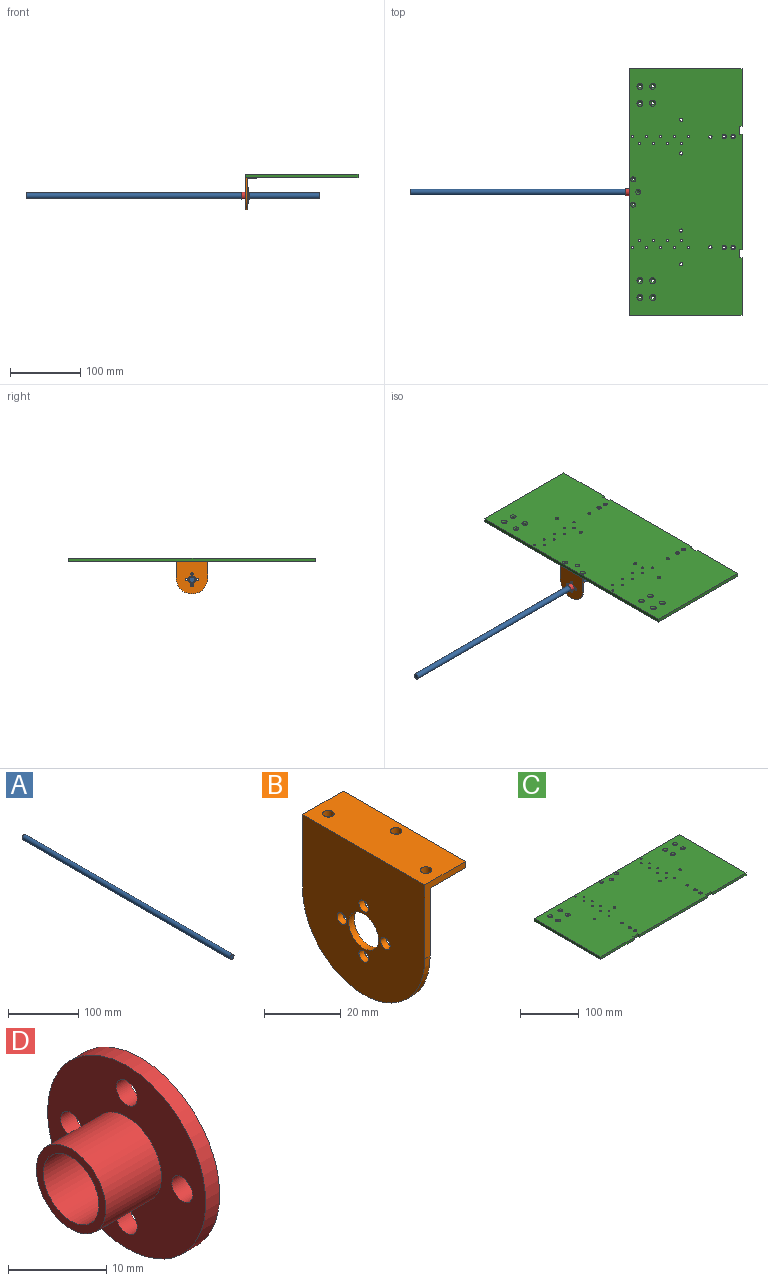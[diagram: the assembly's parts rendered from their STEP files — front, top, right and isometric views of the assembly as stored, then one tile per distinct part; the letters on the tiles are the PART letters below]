
ASSEMBLY  parts=4 mates=3
PART A: 3 faces, bbox 8x418x8 mm
  f0: cylinder r=4mm len=418mm, axis (0,1,0), area 10505.5mm2, adj f1,f2
  f1: plane 8x8mm, normal (0,-1,0), area 50.3mm2, adj f0
  f2: plane 8x8mm, normal (0,1,0), area 50.3mm2, adj f0
PART B: 16 faces, bbox 15x45x46.3 mm
  f0: plane 45x15mm, normal (0,0,1), area 653.8mm2, adj f2,f8,f11,f12,f13,f14,f15
  f1: plane 45x13mm, normal (0,0,-1), area 563.8mm2, adj f2,f8,f10,f12,f13,f14,f15
  f2: plane 23.67x15mm, normal (0,-1,0), area 73.3mm2, adj f0,f1,f3,f10,f11,f12
  f3: cylinder r=22.5mm len=45.01mm, axis (-1,0,0), area 142.9mm2, adj f2,f8,f10,f11
  f4: cylinder r=1.75mm len=3.5mm, axis (-1,0,0), area 22mm2, adj f10,f11
  f5: cylinder r=1.75mm len=3.5mm, axis (-1,0,0), area 22mm2, adj f10,f11
  f6: cylinder r=1.75mm len=3.5mm, axis (-1,0,0), area 22mm2, adj f10,f11
  f7: cylinder r=1.75mm len=3.5mm, axis (-1,0,0), area 22mm2, adj f10,f11
  f8: plane 23.15x15mm, normal (0,1,0), area 72.3mm2, adj f0,f1,f3,f10,f11,f12
  f9: cylinder r=5.5mm len=11mm, axis (-1,0,0), area 69.1mm2, adj f10,f11
  f10: plane 45.01x44.28mm, normal (1,0,0), area 1641.7mm2, adj f1,f2,f3,f4,f5,f6,f7,f8
  f11: plane 46.28x45.01mm, normal (-1,0,0), area 1731.7mm2, adj f0,f2,f3,f4,f5,f6,f7,f8
  f12: plane 45x2mm, normal (1,0,0), area 90mm2, adj f0,f1,f2,f8
  f13: cylinder r=1.5mm len=3mm, axis (0,0,1), area 18.8mm2, adj f0,f1
  f14: cylinder r=1.5mm len=3mm, axis (0,0,1), area 18.8mm2, adj f0,f1
  f15: cylinder r=1.5mm len=3mm, axis (0,0,1), area 18.8mm2, adj f0,f1
PART C: 74 faces, bbox 351x160x5 mm
  f0: plane 81.5x5mm, normal (0,-1,0), area 407.5mm2, adj f1,f4,f46,f71
  f1: plane 351x160mm, normal (0,0,-1), area 55421.6mm2, adj f0,f2,f3,f4,f5,f6,f9,f10
  f2: plane 164x5mm, normal (0,-1,0), area 820mm2, adj f1,f46,f68,f73
  f3: plane 81.5x5mm, normal (0,-1,0), area 407.5mm2, adj f1,f44,f46,f70
  f4: plane 160x5mm, normal (1,0,0), area 800mm2, adj f0,f1,f5,f46
  f5: plane 351x5mm, normal (0,1,0), area 1755mm2, adj f1,f4,f44,f46
  f6: cylinder r=2.25mm len=4.5mm, axis (0,0,-1), area 42.4mm2, adj f1,f56
  f7: cylinder r=2.25mm len=4.5mm, axis (0,0,-1), area 42.4mm2, adj f46,f55
  f8: cylinder r=2.25mm len=4.5mm, axis (0,0,-1), area 42.4mm2, adj f46,f54
  f9: cylinder r=1.5mm len=5mm, axis (0,0,-1), area 47.1mm2, adj f1,f46
  f10: cylinder r=1.5mm len=5mm, axis (0,0,-1), area 47.1mm2, adj f1,f46
  f11: cylinder r=1.5mm len=5mm, axis (0,0,-1), area 47.1mm2, adj f1,f46
  f12: cylinder r=1.5mm len=5mm, axis (0,0,-1), area 47.1mm2, adj f1,f46
  f13: cylinder r=1.5mm len=5mm, axis (0,0,-1), area 47.1mm2, adj f1,f46
  f14: cylinder r=1.5mm len=5mm, axis (0,0,-1), area 47.1mm2, adj f1,f46
  f15: cylinder r=1.5mm len=5mm, axis (0,0,-1), area 47.1mm2, adj f1,f46
  f16: cylinder r=1.5mm len=5mm, axis (0,0,-1), area 47.1mm2, adj f1,f46
  f17: cylinder r=2mm len=4mm, axis (0,0,-1), area 50.3mm2, adj f1,f65
  f18: cylinder r=1.5mm len=5mm, axis (0,0,-1), area 47.1mm2, adj f1,f46
  f19: cylinder r=1.5mm len=5mm, axis (0,0,-1), area 47.1mm2, adj f1,f46
  f20: cylinder r=1.5mm len=5mm, axis (0,0,-1), area 47.1mm2, adj f1,f46
  f21: cylinder r=1.5mm len=5mm, axis (0,0,-1), area 47.1mm2, adj f1,f46
  f22: cylinder r=1.5mm len=5mm, axis (0,0,-1), area 47.1mm2, adj f1,f46
  f23: cylinder r=1.5mm len=5mm, axis (0,0,-1), area 47.1mm2, adj f1,f46
  f24: cylinder r=1.5mm len=5mm, axis (0,0,-1), area 47.1mm2, adj f1,f46
  f25: cylinder r=2mm len=4mm, axis (0,0,-1), area 50.3mm2, adj f1,f64
  f26: cylinder r=2mm len=4mm, axis (0,0,-1), area 50.3mm2, adj f1,f66
  f27: cylinder r=2mm len=4mm, axis (0,0,-1), area 50.3mm2, adj f1,f67
  f28: cylinder r=1.5mm len=5mm, axis (0,0,-1), area 47.1mm2, adj f1,f46
  f29: cylinder r=1.5mm len=5mm, axis (0,0,-1), area 47.1mm2, adj f1,f46
  f30: cylinder r=1.5mm len=5mm, axis (0,0,-1), area 47.1mm2, adj f1,f46
  f31: cylinder r=2.25mm len=4.5mm, axis (0,0,-1), area 42.4mm2, adj f46,f53
  f32: cylinder r=2.25mm len=4.5mm, axis (0,0,-1), area 42.4mm2, adj f46,f50
  f33: cylinder r=2.25mm len=4.5mm, axis (0,0,-1), area 42.4mm2, adj f46,f51
  f34: cylinder r=2.25mm len=4.5mm, axis (0,0,-1), area 42.4mm2, adj f46,f52
  f35: cylinder r=2.25mm len=4.5mm, axis (0,0,-1), area 42.4mm2, adj f1,f59
  f36: cylinder r=2.25mm len=4.5mm, axis (0,0,-1), area 42.4mm2, adj f1,f57
  f37: cylinder r=1.5mm len=3mm, axis (0,0,-1), area 28.3mm2, adj f1,f49
  f38: cylinder r=1.5mm len=3mm, axis (0,0,-1), area 28.3mm2, adj f1,f47
  f39: cylinder r=1.5mm len=3mm, axis (0,0,-1), area 28.3mm2, adj f1,f48
  f40: cylinder r=2.25mm len=4.5mm, axis (0,0,-1), area 42.4mm2, adj f1,f60
  f41: cylinder r=2.25mm len=4.5mm, axis (0,0,-1), area 42.4mm2, adj f1,f62
  f42: cylinder r=2.25mm len=4.5mm, axis (0,0,-1), area 42.4mm2, adj f1,f61
  f43: cylinder r=2.25mm len=4.5mm, axis (0,0,-1), area 42.4mm2, adj f1,f63
  f44: plane 160x5mm, normal (-1,0,0), area 800mm2, adj f1,f3,f5,f46
  f45: cylinder r=2.25mm len=4.5mm, axis (0,0,-1), area 42.4mm2, adj f1,f58
  f46: plane 351x160mm, normal (0,0,1), area 55182.8mm2, adj f0,f2,f3,f4,f5,f7,f8,f9
  f47: cone r=1.5mm half-angle=45deg, axis (0,0,1), area 44.4mm2, adj f38,f46
  f48: cone r=1.5mm half-angle=45deg, axis (0,0,1), area 44.4mm2, adj f39,f46
  f49: cone r=1.5mm half-angle=45deg, axis (0,0,1), area 44.4mm2, adj f37,f46
  f50: cone r=4.25mm half-angle=45deg, axis (0,0,-1), area 57.8mm2, adj f1,f32
  f51: cone r=4.25mm half-angle=45deg, axis (0,0,-1), area 57.8mm2, adj f1,f33
  f52: cone r=4.25mm half-angle=45deg, axis (0,0,-1), area 57.8mm2, adj f1,f34
  f53: cone r=2.25mm half-angle=45deg, axis (0,0,-1), area 57.8mm2, adj f1,f31
  f54: cone r=2.25mm half-angle=45deg, axis (0,0,-1), area 57.8mm2, adj f1,f8
  f55: cone r=2.25mm half-angle=45deg, axis (0,0,-1), area 57.8mm2, adj f1,f7
  f56: cone r=4.25mm half-angle=45deg, axis (0,0,1), area 57.8mm2, adj f6,f46
  f57: cone r=4.25mm half-angle=45deg, axis (0,0,1), area 57.8mm2, adj f36,f46
  f58: cone r=4.25mm half-angle=45deg, axis (0,0,1), area 57.8mm2, adj f45,f46
  f59: cone r=4.25mm half-angle=45deg, axis (0,0,1), area 57.8mm2, adj f35,f46
  f60: cone r=2.25mm half-angle=45deg, axis (0,0,1), area 57.8mm2, adj f40,f46
  f61: cone r=2.25mm half-angle=45deg, axis (0,0,1), area 57.8mm2, adj f42,f46
  f62: cone r=2.25mm half-angle=45deg, axis (0,0,1), area 57.8mm2, adj f41,f46
  f63: cone r=2.25mm half-angle=45deg, axis (0,0,1), area 57.8mm2, adj f43,f46
  f64: cone r=3mm half-angle=45deg, axis (0,0,1), area 22.2mm2, adj f25,f46
  f65: cone r=3mm half-angle=45deg, axis (0,0,1), area 22.2mm2, adj f17,f46
  f66: cone r=2mm half-angle=45deg, axis (0,0,1), area 22.2mm2, adj f26,f46
  f67: cone r=2mm half-angle=45deg, axis (0,0,1), area 22.2mm2, adj f27,f46
  f68: plane 5x3mm, normal (-1,0,0), area 15mm2, adj f1,f2,f46,f69
  f69: plane 12x5mm, normal (0,-1,0), area 60mm2, adj f1,f46,f68,f70
  f70: plane 5x3mm, normal (1,0,0), area 15mm2, adj f1,f3,f46,f69
  f71: plane 5x3mm, normal (-1,0,0), area 15mm2, adj f0,f1,f46,f72
  f72: plane 12x5mm, normal (0,-1,0), area 60mm2, adj f1,f46,f71,f73
  f73: plane 5x3mm, normal (1,0,0), area 15mm2, adj f1,f2,f46,f72
PART D: 12 faces, bbox 11.5x22.7x22.7 mm
  f0: cylinder r=1.5mm len=3mm, axis (-1,0,0), area 18.8mm2, adj f5,f6
  f1: cylinder r=1.5mm len=3mm, axis (-1,0,0), area 18.8mm2, adj f5,f6
  f2: cylinder r=1.5mm len=3mm, axis (-1,0,0), area 18.8mm2, adj f5,f6
  f3: cylinder r=1.5mm len=3mm, axis (-1,0,0), area 18.8mm2, adj f5,f6
  f4: cylinder r=11.37mm len=22.75mm, axis (-1,0,0), area 142.9mm2, adj f5,f6
  f5: plane 22.75x22.75mm, normal (1,0,0), area 299.6mm2, adj f0,f1,f2,f3,f4,f9
  f6: plane 22.75x22.75mm, normal (-1,0,0), area 299.6mm2, adj f0,f1,f2,f3,f4,f7
  f7: cylinder r=5mm len=10mm, axis (1,0,0), area 251.3mm2, adj f6,f8
  f8: plane 10x10mm, normal (-1,0,0), area 28.3mm2, adj f7,f11
  f9: cylinder r=5mm len=10mm, axis (-1,0,0), area 47.1mm2, adj f5,f10
  f10: plane 10x10mm, normal (1,0,0), area 28.3mm2, adj f9,f11
  f11: cylinder r=4mm len=11.5mm, axis (1,0,0), area 289mm2, adj f8,f10
PLACE A rot(axis=(-0.69,-0.69,-0.23),154.2deg) t=(300.66,21.61,-244.82)mm
PLACE B t=(196.12,21.61,-244.82)mm
PLACE C rot(axis=(0,0,1),90deg) t=(276.12,21.61,-218.82)mm
PLACE D t=(198.12,21.61,-244.82)mm
MATE fastened B.f9 <-> D.f7  axis (1,0,0) through (198.12,21.61,-244.82)mm
MATE fastened C.f38 <-> B.f14  axis (0,0,-1) through (208.12,21.61,-218.82)mm
MATE cylindrical A.f0 <-> D.f7  axis (-1,0,0) through (-117.34,21.61,-244.82)mm
